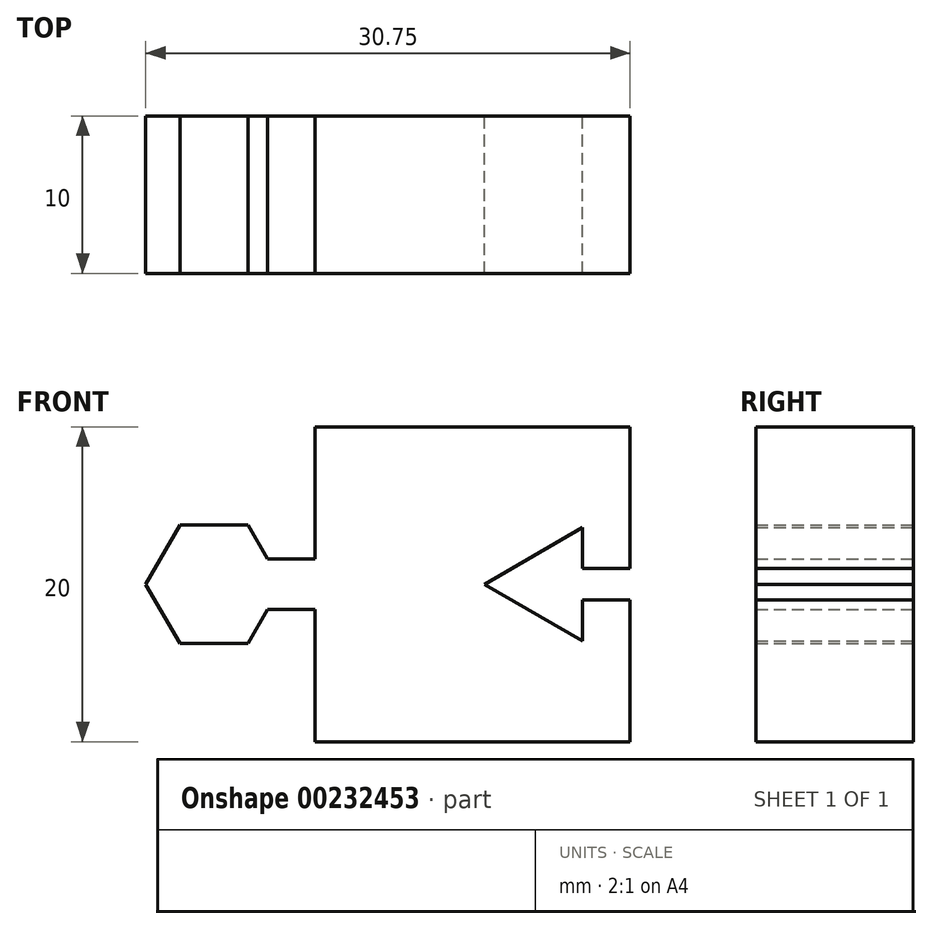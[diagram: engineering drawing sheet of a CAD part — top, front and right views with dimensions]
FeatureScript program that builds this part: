
annotation { "Feature Type Name" : "Feature", "Feature Type Description" : "" }
export const myFeature = defineFeature(function(context is Context, id is Id, definition is map)
    precondition{}
    {
        {
            var Q0;
            Q0=qCreatedBy(makeId("Front.planeOp"),FACE);
            var sketch = newSketch(context, id + "F0", { "sketchPlane" : qUnion([Q0])});
            skLineSegment(sketch, "E0.bottom", {"start": v(-19.16, 23.18) * mm, "end": v(0.84, 23.18) * mm});
            skLineSegment(sketch, "E0.top", {"start": v(-19.16, 3.18) * mm, "end": v(0.84, 3.18) * mm});
            skLineSegment(sketch, "E0.left", {"start": v(-19.16, 23.18) * mm, "end": v(-19.16, 14.78) * mm});
            skLineSegment(sketch, "E0.right", {"start": v(0.84, 23.18) * mm, "end": v(0.84, 3.18) * mm});
            skLineSegment(sketch, "E1.bottom", {"start": v(-19.16, 14.78) * mm, "end": v(-22.16, 14.78) * mm});
            skLineSegment(sketch, "E1.top", {"start": v(-19.16, 11.58) * mm, "end": v(-22.16, 11.58) * mm});
            skPoint(sketch, "E2", {"position": v(-22.16, 13.18) * mm});
            skPoint(sketch, "E3", {"position": v(-19.16, 13.18) * mm});
            skLineSegment(sketch, "E4.trimOffspring", {"start": v(-19.16, 11.58) * mm, "end": v(-19.16, 3.18) * mm});
            skLineSegment(sketch, "E5.0", {"start": v(-2.16, 9.58) * mm, "end": v(-8.4, 13.18) * mm});
            skLineSegment(sketch, "E5.1", {"start": v(-8.4, 13.18) * mm, "end": v(-2.16, 16.78) * mm});
            skLineSegment(sketch, "E5.2", {"start": v(-2.16, 16.78) * mm, "end": v(-2.16, 14.18) * mm});
            skPoint(sketch, "E5.0.midPoint", {"position": v(-5.28, 11.38) * mm});
            skPoint(sketch, "E6", {"position": v(-4.24, 13.18) * mm});
            skPoint(sketch, "E7", {"position": v(-2.16, 13.18) * mm});
            skPoint(sketch, "E8", {"position": v(0.84, 13.18) * mm});
            skLineSegment(sketch, "E9.bottom", {"start": v(-2.16, 14.18) * mm, "end": v(0.84, 14.18) * mm});
            skLineSegment(sketch, "E9.top", {"start": v(-2.16, 12.18) * mm, "end": v(0.84, 12.18) * mm});
            skLineSegment(sketch, "E10.0", {"start": v(-22.16, 11.58) * mm, "end": v(-23.4, 9.42) * mm});
            skLineSegment(sketch, "E10.1", {"start": v(-23.4, 9.42) * mm, "end": v(-27.75, 9.42) * mm});
            skLineSegment(sketch, "E10.2", {"start": v(-27.75, 9.42) * mm, "end": v(-29.91, 13.18) * mm});
            skLineSegment(sketch, "E10.3", {"start": v(-29.91, 13.18) * mm, "end": v(-27.75, 16.94) * mm});
            skLineSegment(sketch, "E10.4", {"start": v(-27.75, 16.94) * mm, "end": v(-23.4, 16.94) * mm});
            skLineSegment(sketch, "E10.5", {"start": v(-23.4, 16.94) * mm, "end": v(-22.16, 14.78) * mm});
            skPoint(sketch, "E10.0.midPoint", {"position": v(-22.32, 11.3) * mm});
            skPoint(sketch, "E11", {"position": v(-43.82, 13.18) * mm});
            skPoint(sketch, "E12", {"position": v(-22.32, 15.06) * mm});
            skPoint(sketch, "E13.orphan", {"position": v(-21.24, 13.18) * mm});
            skLineSegment(sketch, "E14.trimOffspring", {"start": v(-2.16, 12.18) * mm, "end": v(-2.16, 9.58) * mm});
            skSolve(sketch);
        }
        {
            var Q0;
            {var subQ0=sQuery(id+"F0.wireOp",EDGE,"E0.bottom");Q0=makeQuery(id+"F0.imprint","IMPRINT",FACE,{"disambiguationData":[TD([[makeQuery(id+"F0.imprint","IMPRINT",EDGE,{"derivedFrom":subQ0}),-1.0]])]});}
            extrude(context, id + "F1", {"entities" : qUnion([Q0]), "depth" : 10 * mm});
        }
    });
